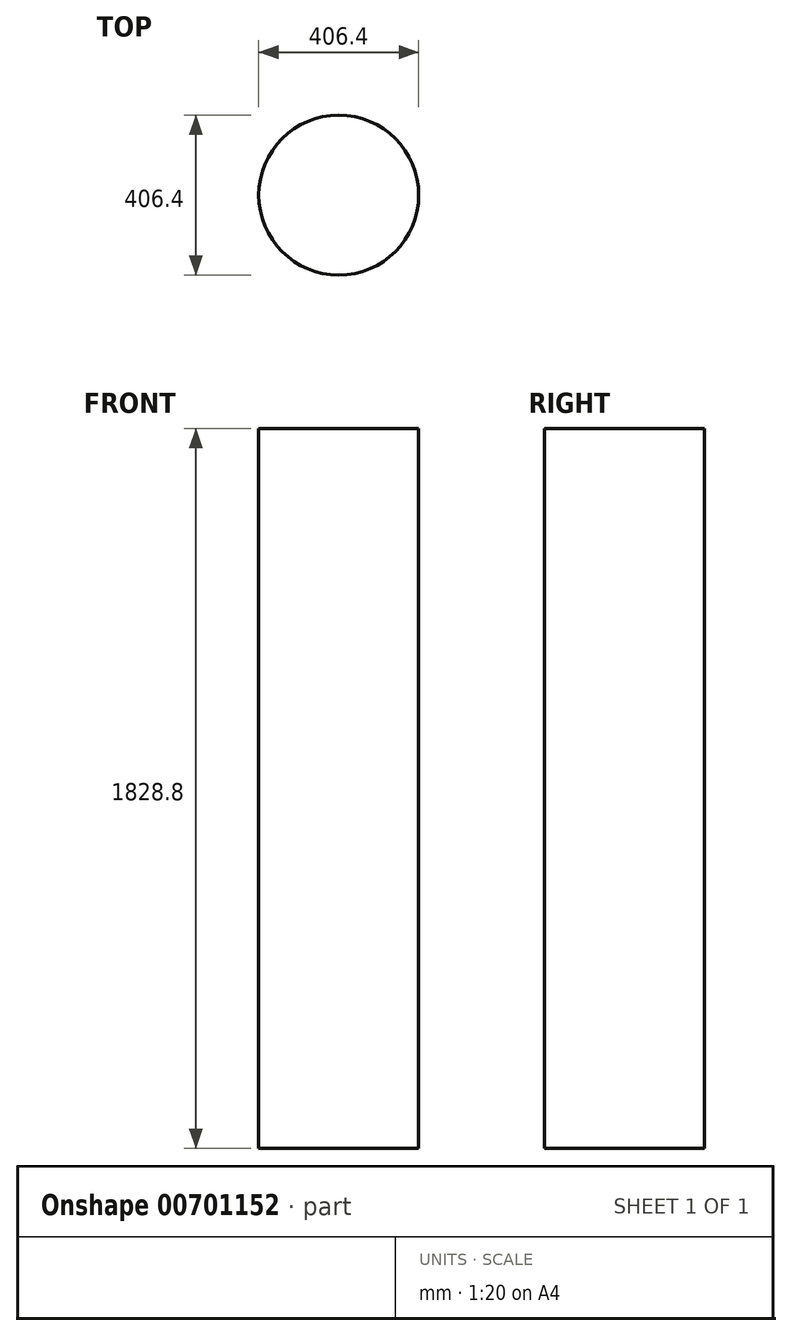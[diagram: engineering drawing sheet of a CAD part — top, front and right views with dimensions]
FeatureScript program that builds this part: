
annotation { "Feature Type Name" : "Feature", "Feature Type Description" : "" }
export const myFeature = defineFeature(function(context is Context, id is Id, definition is map)
    precondition{}
    {
        {
            var Q0;
            Q0=qCreatedBy(makeId("Top.planeOp"),FACE);
            var sketch = newSketch(context, id + "F0", { "sketchPlane" : qUnion([Q0])});
            skCircle(sketch, "E0", {"center": v(0, 0) * mm, "radius": 203.2 * mm});
            skSolve(sketch);
        }
        {
            var Q0;
            Q0 = qSketchRegion(id + "F0", true);
            extrude(context, id + "F1", {"entities" : qUnion([Q0]), "depth" : 1828.8 * mm, "offsetDistance" : 25.4 * mm});
        }
    });
